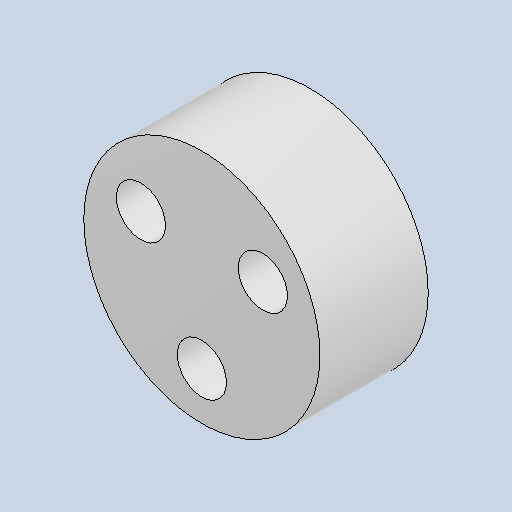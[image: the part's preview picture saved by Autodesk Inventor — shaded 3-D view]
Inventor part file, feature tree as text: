
AUTODESK INVENTOR PART (.ipt)
format: ipt  version: 2023 (Build 270158000, 158)  size: 104,448 bytes
history: native  units: mm
features: other x3, sketch x1
ambient origin geometry x8: Origin, YZ Plane, XZ Plane, XY Plane, X Axis, Y Axis, Z Axis, Center Point
bodies: Solid1 (feature_tree)
feature tree (4):
  other  "カム3.ipt"
  other  "Solid1::カム3.ipt"
  other  "TaggingFeature1"
  sketch  "Sketch1"  dims[d0=10.0mm]
